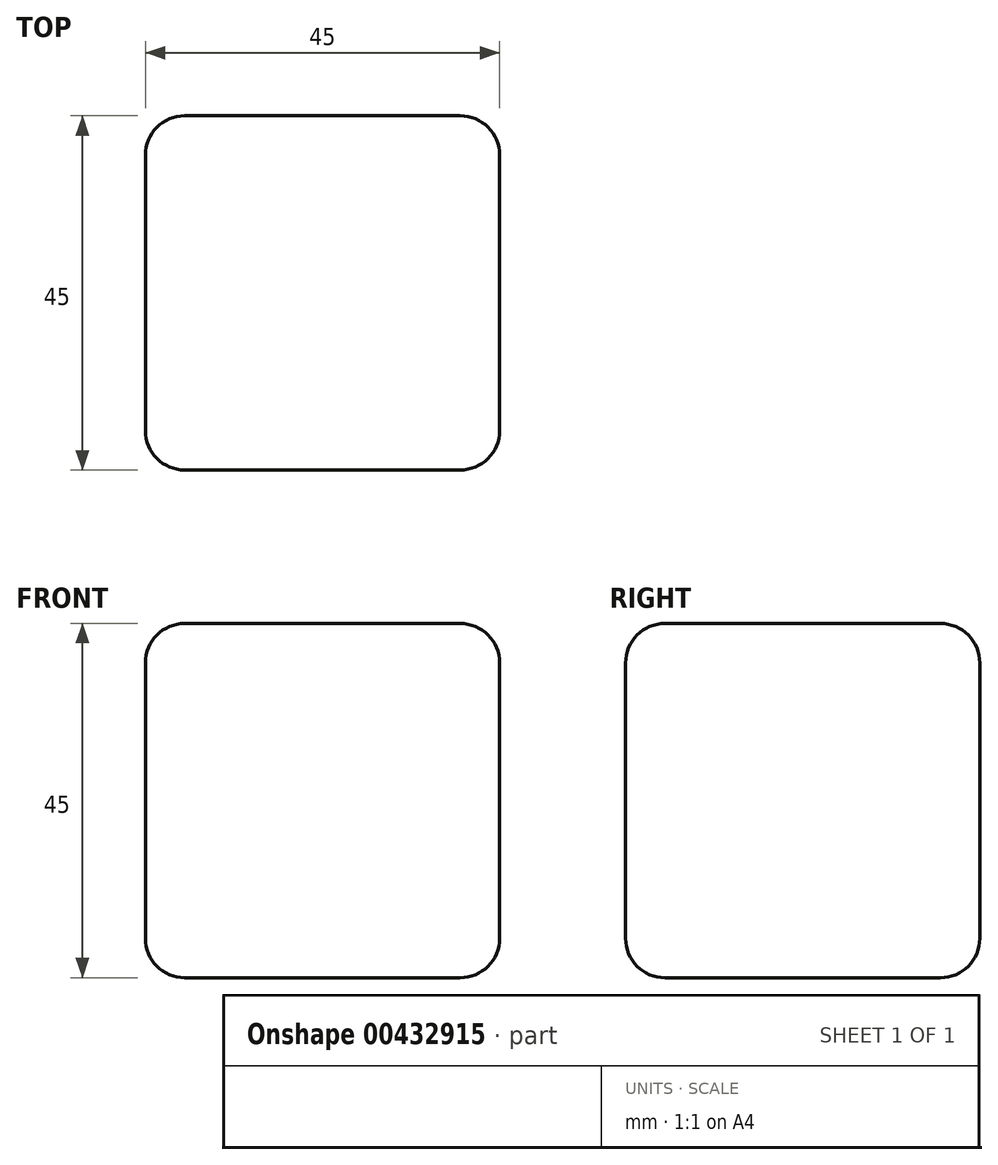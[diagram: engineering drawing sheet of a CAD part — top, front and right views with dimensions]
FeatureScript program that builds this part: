
annotation { "Feature Type Name" : "Feature", "Feature Type Description" : "" }
export const myFeature = defineFeature(function(context is Context, id is Id, definition is map)
    precondition{}
    {
        {
            var Q0;
            Q0=qCreatedBy(makeId("Front.planeOp"),FACE);
            var sketch = newSketch(context, id + "F0", { "sketchPlane" : qUnion([Q0])});
            skLineSegment(sketch, "E0.bottom", {"start": v(0, 0) * mm, "end": v(-45, 0) * mm});
            skLineSegment(sketch, "E0.top", {"start": v(0, 45) * mm, "end": v(-45, 45) * mm});
            skLineSegment(sketch, "E0.left", {"start": v(0, 0) * mm, "end": v(0, 45) * mm});
            skLineSegment(sketch, "E0.right", {"start": v(-45, 0) * mm, "end": v(-45, 45) * mm});
            skSolve(sketch);
        }
        {
            var Q0;
            Q0=qSketchRegion(id+"F0",true);
            extrude(context, id + "F1", {"entities" : qUnion([Q0]), "depth" : 45 * mm});
        }
        {
            var Q0;
            Q0=makeQuery(id+"F1.opExtrude","CAP_FACE",FACE,{"disambiguationData":[OSD([sQuery(id+"F0.wireOp",EDGE,"E0.bottom"),sQuery(id+"F0.wireOp",EDGE,"E0.top"),sQuery(id+"F0.wireOp",EDGE,"E0.left"),sQuery(id+"F0.wireOp",EDGE,"E0.right")])],"isStart":false});
            var Q1;
            Q1=makeQuery(id+"F1.opExtrude","SWEPT_FACE",FACE,{"disambiguationData":[OSD([sQuery(id+"F0.wireOp",EDGE,"E0.right")])]});
            var Q2;
            Q2=makeQuery(id+"F1.opExtrude","SWEPT_FACE",FACE,{"disambiguationData":[OSD([sQuery(id+"F0.wireOp",EDGE,"E0.top")])]});
            var Q3;
            Q3=makeQuery(id+"F1.opExtrude","SWEPT_FACE",FACE,{"disambiguationData":[OSD([sQuery(id+"F0.wireOp",EDGE,"E0.left")])]});
            var Q4;
            Q4=makeQuery(id+"F1.opExtrude","CAP_FACE",FACE,{"disambiguationData":[OSD([sQuery(id+"F0.wireOp",EDGE,"E0.bottom"),sQuery(id+"F0.wireOp",EDGE,"E0.top"),sQuery(id+"F0.wireOp",EDGE,"E0.left"),sQuery(id+"F0.wireOp",EDGE,"E0.right")])],"isStart":true});
            fillet(context, id + "F2", {"entities" : qUnion([Q0, Q1, Q2, Q3, Q4]), "radius" : 5 * mm, "tangentPropagation" : true, "allowEdgeOverflow" : false});
        }
    });
